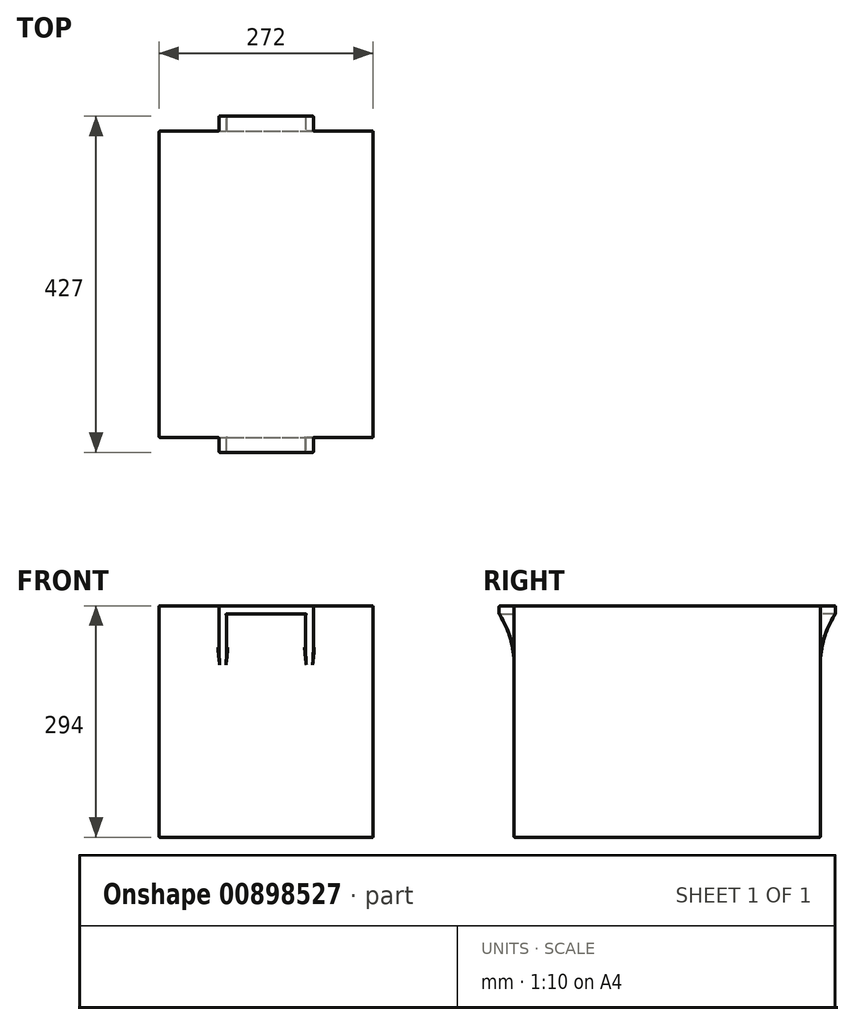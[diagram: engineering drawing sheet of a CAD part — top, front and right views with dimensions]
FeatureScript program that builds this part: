
annotation { "Feature Type Name" : "Feature", "Feature Type Description" : "" }
export const myFeature = defineFeature(function(context is Context, id is Id, definition is map)
    precondition{}
    {
        {
            var Q0;
            Q0=qCreatedBy(makeId("Top.planeOp"),FACE);
            var sketch = newSketch(context, id + "F0", { "sketchPlane" : qUnion([Q0])});
            skLineSegment(sketch, "E0.bottom", {"start": v(-136, 194.5) * mm, "end": v(0, 194.5) * mm});
            skLineSegment(sketch, "E0.left", {"start": v(-136, 194.5) * mm, "end": v(-136, 0) * mm});
            skLineSegment(sketch, "E1", {"start": v(0, 194.5) * mm, "end": v(0, 213.5) * mm});
            skLineSegment(sketch, "E2", {"start": v(0, 213.5) * mm, "end": v(0, 194.5) * mm});
            skLineSegment(sketch, "E3.right", {"start": v(-60, 213.5) * mm, "end": v(-60, 194.5) * mm});
            skPoint(sketch, "E3.middle", {"position": v(0, 194.5) * mm});
            skLineSegment(sketch, "E4", {"start": v(-136, 0) * mm, "end": v(0, 0) * mm});
            skLineSegment(sketch, "E5", {"start": v(0, 0) * mm, "end": v(0, 213.5) * mm});
            skLineSegment(sketch, "E6", {"start": v(-60, 213.5) * mm, "end": v(0, 213.5) * mm});
            skLineSegment(sketch, "E7", {"start": v(-60, 213.5) * mm, "end": v(-50, 213.5) * mm});
            skLineSegment(sketch, "E8", {"start": v(-50, 213.5) * mm, "end": v(-50, 194.5) * mm});
            skLineSegment(sketch, "E9", {"start": v(-50, 194.5) * mm, "end": v(-50, 213.5) * mm});
            skSolve(sketch);
        }
        {
            var Q0;
            {var subQ0=sQuery(id+"F0.wireOp",EDGE,"E0.left");Q0=makeQuery(id+"F0.imprint","IMPRINT",FACE,{"disambiguationData":[TD([[makeQuery(id+"F0.imprint","IMPRINT",EDGE,{"derivedFrom":subQ0}),1.0]])]});}
            extrude(context, id + "F1", {"entities" : qUnion([Q0]), "oppositeDirection" : true, "depth" : 294 * mm, "offsetDistance" : 25 * mm});
        }
        {
            var Q0;
            {var subQ4=sQuery(id+"F0.wireOp",EDGE,"E6");Q0=makeQuery(id+"F0.imprint","IMPRINT",FACE,{"disambiguationData":[TD([[makeQuery(id+"F0.imprint","IMPRINT",EDGE,{"derivedFrom":subQ4}),-1.0]])]});}
            extrude(context, id + "F2", {"entities" : qUnion([Q0]), "operationType" : NewBodyOperationType.ADD, "oppositeDirection" : true, "depth" : 10 * mm, "offsetDistance" : 25 * mm});
        }
        {
            var Q0;
            {var subQ0=sQuery(id+"F0.wireOp",EDGE,"E3.right");Q0=makeQuery(id+"F0.imprint","IMPRINT",FACE,{"disambiguationData":[TD([[makeQuery(id+"F0.imprint","IMPRINT",EDGE,{"derivedFrom":subQ0}),1.0]])]});}
            extrude(context, id + "F3", {"entities" : qUnion([Q0]), "operationType" : NewBodyOperationType.ADD, "oppositeDirection" : true, "depth" : 75 * mm, "offsetDistance" : 25 * mm});
        }
        {
            var Q0;
            Q0=makeQuery(id+"F3.opExtrude","SWEPT_FACE",FACE,{"disambiguationData":[OSD([sQuery(id+"F0.wireOp",EDGE,"E3.right")])]});
            var sketch = newSketch(context, id + "F4", { "sketchPlane" : qUnion([Q0])});
            skLineSegment(sketch, "E10.bottom", {"start": v(-213.5, 0) * mm, "end": v(-194.5, 0) * mm});
            skLineSegment(sketch, "E10.top", {"start": v(-213.5, -10) * mm, "end": v(-194.5, -10) * mm});
            skLineSegment(sketch, "E11.right", {"start": v(-194.5, -75) * mm, "end": v(-194.5, -10) * mm});
            skArc(sketch, "E12", {"start": v(-194.5, -75) * mm, "mid": v(-199.35, -41.14) * mm, "end": v(-213.5, -10) * mm});
            skSolve(sketch);
        }
        {
            var Q0;
            {var subQ0=sQuery(id+"F4.wireOp",EDGE,"E12");Q0=makeQuery(id+"F4.imprint","IMPRINT",FACE,{"disambiguationData":[TD([[makeQuery(id+"F4.imprint","IMPRINT",EDGE,{"derivedFrom":subQ0}),1.0]])]});}
            extrude(context, id + "F5", {"entities" : qUnion([Q0]), "operationType" : NewBodyOperationType.REMOVE, "oppositeDirection" : true, "depth" : 10 * mm, "offsetDistance" : 25 * mm});
        }
        {
            var Q0;
            Q0=makeQuery(id+"F1.opExtrude","SWEPT_BODY",BODY,{"disambiguationData":[OSD([sQuery(id+"F0.wireOp",EDGE,"E0.bottom"),sQuery(id+"F0.wireOp",EDGE,"E0.left"),sQuery(id+"F0.wireOp",EDGE,"E4"),sQuery(id+"F0.wireOp",EDGE,"E5")])]});
            var Q1;
            {var subQ0=sQuery(id+"F0.wireOp",EDGE,"E5");Q1=makeQuery(id+"F2.boolean.opBoolean","MERGE",FACE,{"derivedFrom":[makeQuery(id+"F1.opExtrude","SWEPT_FACE",FACE,{"disambiguationData":[OSD([subQ0])]}),makeQuery(id+"F2.opExtrude","SWEPT_FACE",FACE,{"disambiguationData":[OSD([subQ0])]})]});}
            mirror(context, id + "F6", {"operationType" : NewBodyOperationType.ADD, "entities" : qUnion([Q0]), "mirrorPlane" : qUnion([Q1])});
        }
        {
            var Q0;
            Q0=makeQuery(id+"F1.opExtrude","SWEPT_BODY",BODY,{"disambiguationData":[OSD([sQuery(id+"F0.wireOp",EDGE,"E0.bottom"),sQuery(id+"F0.wireOp",EDGE,"E0.left"),sQuery(id+"F0.wireOp",EDGE,"E4"),sQuery(id+"F0.wireOp",EDGE,"E5")])]});
            var Q1;
            {var subQ0=makeQuery(id+"F1.opExtrude","SWEPT_FACE",FACE,{"disambiguationData":[OSD([sQuery(id+"F0.wireOp",EDGE,"E4")])]});Q1=makeQuery(id+"F6.boolean.opBoolean","MERGE",FACE,{"derivedFrom":[subQ0,makeQuery(id+"F6.opPattern","COPY",FACE,{"derivedFrom":subQ0,"instanceName":"1"})]});}
            mirror(context, id + "F7", {"operationType" : NewBodyOperationType.ADD, "entities" : qUnion([Q0]), "mirrorPlane" : qUnion([Q1])});
        }
        {
            var Q0;
            {var subQ0=makeQuery(id+"F1.opExtrude","SWEPT_FACE",FACE,{"disambiguationData":[OSD([sQuery(id+"F0.wireOp",EDGE,"E0.bottom")])]});Q0=makeQuery(id+"F6.boolean.opBoolean","MERGE",FACE,{"derivedFrom":[subQ0,makeQuery(id+"F6.opPattern","COPY",FACE,{"derivedFrom":subQ0,"instanceName":"1"})]});}
            var Q1;
            Q1=makeQuery(id+"F6.opPattern","COPY",FACE,{"derivedFrom":makeQuery(id+"F5.boolean.opBoolean","COPY",FACE,{"derivedFrom":makeQuery(id+"F5.opExtrude","SWEPT_FACE",FACE,{"disambiguationData":[OSD([sQuery(id+"F4.wireOp",EDGE,"E12")])]})}),"instanceName":"1"});
            var Q2;
            Q2=makeQuery(id+"F6.opPattern","COPY",FACE,{"derivedFrom":makeQuery(id+"F3.opExtrude","SWEPT_FACE",FACE,{"disambiguationData":[OSD([sQuery(id+"F0.wireOp",EDGE,"E9")])]}),"instanceName":"1"});
            var Q3;
            {var subQ0=makeQuery(id+"F2.opExtrude","CAP_FACE",FACE,{"disambiguationData":[OSD([sQuery(id+"F0.wireOp",EDGE,"E0.bottom"),sQuery(id+"F0.wireOp",EDGE,"E5"),sQuery(id+"F0.wireOp",EDGE,"E6"),sQuery(id+"F0.wireOp",EDGE,"E9")])],"isStart":false});Q3=makeQuery(id+"F6.boolean.opBoolean","MERGE",FACE,{"derivedFrom":[subQ0,makeQuery(id+"F6.opPattern","COPY",FACE,{"derivedFrom":subQ0,"instanceName":"1"})]});}
            var Q4;
            {var subQ0=makeQuery(id+"F3.boolean.opBoolean","MERGE",FACE,{"derivedFrom":[makeQuery(id+"F2.opExtrude","SWEPT_FACE",FACE,{"disambiguationData":[OSD([sQuery(id+"F0.wireOp",EDGE,"E6")])]}),makeQuery(id+"F3.opExtrude","SWEPT_FACE",FACE,{"disambiguationData":[OSD([sQuery(id+"F0.wireOp",EDGE,"E7")])]})]});Q4=makeQuery(id+"F6.boolean.opBoolean","MERGE",FACE,{"derivedFrom":[subQ0,makeQuery(id+"F6.opPattern","COPY",FACE,{"derivedFrom":subQ0,"instanceName":"1"})]});}
            var Q5;
            Q5=makeQuery(id+"F5.boolean.opBoolean","COPY",FACE,{"derivedFrom":makeQuery(id+"F5.opExtrude","SWEPT_FACE",FACE,{"disambiguationData":[OSD([sQuery(id+"F4.wireOp",EDGE,"E12")])]})});
            var Q6;
            Q6=makeQuery(id+"F3.opExtrude","SWEPT_FACE",FACE,{"disambiguationData":[OSD([sQuery(id+"F0.wireOp",EDGE,"E9")])]});
            var Q7;
            Q7=makeQuery(id+"F6.opPattern","COPY",FACE,{"derivedFrom":makeQuery(id+"F3.opExtrude","SWEPT_FACE",FACE,{"disambiguationData":[OSD([sQuery(id+"F0.wireOp",EDGE,"E3.right")])]}),"instanceName":"1"});
            var Q8;
            Q8=makeQuery(id+"F3.opExtrude","SWEPT_FACE",FACE,{"disambiguationData":[OSD([sQuery(id+"F0.wireOp",EDGE,"E3.right")])]});
            var Q9;
            {var subQ0=sQuery(id+"F0.wireOp",EDGE,"E9");var subQ1=sQuery(id+"F0.wireOp",EDGE,"E0.bottom");var subQ2=sQuery(id+"F0.wireOp",EDGE,"E5");var subQ3=makeQuery(id+"F3.boolean.opBoolean","MERGE",FACE,{"derivedFrom":[makeQuery(id+"F2.boolean.opBoolean","MERGE",FACE,{"derivedFrom":[makeQuery(id+"F1.opExtrude","CAP_FACE",FACE,{"disambiguationData":[OSD([subQ1,sQuery(id+"F0.wireOp",EDGE,"E0.left"),sQuery(id+"F0.wireOp",EDGE,"E4"),subQ2])],"isStart":true}),makeQuery(id+"F2.opExtrude","CAP_FACE",FACE,{"disambiguationData":[OSD([subQ1,subQ2,sQuery(id+"F0.wireOp",EDGE,"E6"),subQ0])],"isStart":true})]}),makeQuery(id+"F3.opExtrude","CAP_FACE",FACE,{"disambiguationData":[OSD([subQ1,sQuery(id+"F0.wireOp",EDGE,"E3.right"),sQuery(id+"F0.wireOp",EDGE,"E7"),subQ0])],"isStart":true})]});var subQ4=makeQuery(id+"F6.boolean.opBoolean","MERGE",FACE,{"derivedFrom":[subQ3,makeQuery(id+"F6.opPattern","COPY",FACE,{"derivedFrom":subQ3,"instanceName":"1"})]});Q9=makeQuery(id+"F7.boolean.opBoolean","MERGE",FACE,{"derivedFrom":[subQ4,makeQuery(id+"F7.opPattern","COPY",FACE,{"derivedFrom":subQ4,"instanceName":"1"})]});}
            var Q10;
            {var subQ0=makeQuery(id+"F1.opExtrude","SWEPT_FACE",FACE,{"disambiguationData":[OSD([sQuery(id+"F0.wireOp",EDGE,"E0.left")])]});Q10=makeQuery(id+"F7.boolean.opBoolean","MERGE",FACE,{"derivedFrom":[subQ0,makeQuery(id+"F7.opPattern","COPY",FACE,{"derivedFrom":subQ0,"instanceName":"1"})]});}
            var Q11;
            {var subQ0=makeQuery(id+"F6.opPattern","COPY",FACE,{"derivedFrom":makeQuery(id+"F1.opExtrude","SWEPT_FACE",FACE,{"disambiguationData":[OSD([sQuery(id+"F0.wireOp",EDGE,"E0.left")])]}),"instanceName":"1"});Q11=makeQuery(id+"F7.boolean.opBoolean","MERGE",FACE,{"derivedFrom":[subQ0,makeQuery(id+"F7.opPattern","COPY",FACE,{"derivedFrom":subQ0,"instanceName":"1"})]});}
            var Q12;
            {var subQ0=makeQuery(id+"F1.opExtrude","SWEPT_FACE",FACE,{"disambiguationData":[OSD([sQuery(id+"F0.wireOp",EDGE,"E0.bottom")])]});Q12=makeQuery(id+"F7.opPattern","COPY",FACE,{"derivedFrom":makeQuery(id+"F6.boolean.opBoolean","MERGE",FACE,{"derivedFrom":[subQ0,makeQuery(id+"F6.opPattern","COPY",FACE,{"derivedFrom":subQ0,"instanceName":"1"})]}),"instanceName":"1"});}
            var Q13;
            Q13=makeQuery(id+"F7.opPattern","COPY",FACE,{"derivedFrom":makeQuery(id+"F6.opPattern","COPY",FACE,{"derivedFrom":makeQuery(id+"F3.opExtrude","SWEPT_FACE",FACE,{"disambiguationData":[OSD([sQuery(id+"F0.wireOp",EDGE,"E3.right")])]}),"instanceName":"1"}),"instanceName":"1"});
            var Q14;
            Q14=makeQuery(id+"F7.opPattern","COPY",FACE,{"derivedFrom":makeQuery(id+"F6.opPattern","COPY",FACE,{"derivedFrom":makeQuery(id+"F5.boolean.opBoolean","COPY",FACE,{"derivedFrom":makeQuery(id+"F5.opExtrude","SWEPT_FACE",FACE,{"disambiguationData":[OSD([sQuery(id+"F4.wireOp",EDGE,"E12")])]})}),"instanceName":"1"}),"instanceName":"1"});
            var Q15;
            {var subQ0=makeQuery(id+"F3.boolean.opBoolean","MERGE",FACE,{"derivedFrom":[makeQuery(id+"F2.opExtrude","SWEPT_FACE",FACE,{"disambiguationData":[OSD([sQuery(id+"F0.wireOp",EDGE,"E6")])]}),makeQuery(id+"F3.opExtrude","SWEPT_FACE",FACE,{"disambiguationData":[OSD([sQuery(id+"F0.wireOp",EDGE,"E7")])]})]});Q15=makeQuery(id+"F7.opPattern","COPY",FACE,{"derivedFrom":makeQuery(id+"F6.boolean.opBoolean","MERGE",FACE,{"derivedFrom":[subQ0,makeQuery(id+"F6.opPattern","COPY",FACE,{"derivedFrom":subQ0,"instanceName":"1"})]}),"instanceName":"1"});}
            var Q16;
            Q16=makeQuery(id+"F7.opPattern","COPY",FACE,{"derivedFrom":makeQuery(id+"F6.opPattern","COPY",FACE,{"derivedFrom":makeQuery(id+"F3.opExtrude","SWEPT_FACE",FACE,{"disambiguationData":[OSD([sQuery(id+"F0.wireOp",EDGE,"E9")])]}),"instanceName":"1"}),"instanceName":"1"});
            var Q17;
            {var subQ0=makeQuery(id+"F2.opExtrude","CAP_FACE",FACE,{"disambiguationData":[OSD([sQuery(id+"F0.wireOp",EDGE,"E0.bottom"),sQuery(id+"F0.wireOp",EDGE,"E5"),sQuery(id+"F0.wireOp",EDGE,"E6"),sQuery(id+"F0.wireOp",EDGE,"E9")])],"isStart":false});Q17=makeQuery(id+"F7.opPattern","COPY",FACE,{"derivedFrom":makeQuery(id+"F6.boolean.opBoolean","MERGE",FACE,{"derivedFrom":[subQ0,makeQuery(id+"F6.opPattern","COPY",FACE,{"derivedFrom":subQ0,"instanceName":"1"})]}),"instanceName":"1"});}
            var Q18;
            Q18=makeQuery(id+"F7.opPattern","COPY",FACE,{"derivedFrom":makeQuery(id+"F3.opExtrude","SWEPT_FACE",FACE,{"disambiguationData":[OSD([sQuery(id+"F0.wireOp",EDGE,"E9")])]}),"instanceName":"1"});
            var Q19;
            Q19=makeQuery(id+"F7.opPattern","COPY",FACE,{"derivedFrom":makeQuery(id+"F5.boolean.opBoolean","COPY",FACE,{"derivedFrom":makeQuery(id+"F5.opExtrude","SWEPT_FACE",FACE,{"disambiguationData":[OSD([sQuery(id+"F4.wireOp",EDGE,"E12")])]})}),"instanceName":"1"});
            var Q20;
            Q20=makeQuery(id+"F7.opPattern","COPY",FACE,{"derivedFrom":makeQuery(id+"F3.opExtrude","SWEPT_FACE",FACE,{"disambiguationData":[OSD([sQuery(id+"F0.wireOp",EDGE,"E3.right")])]}),"instanceName":"1"});
            var Q21;
            {var subQ0=makeQuery(id+"F1.opExtrude","CAP_FACE",FACE,{"disambiguationData":[OSD([sQuery(id+"F0.wireOp",EDGE,"E0.bottom"),sQuery(id+"F0.wireOp",EDGE,"E0.left"),sQuery(id+"F0.wireOp",EDGE,"E4"),sQuery(id+"F0.wireOp",EDGE,"E5")])],"isStart":false});var subQ1=makeQuery(id+"F6.boolean.opBoolean","MERGE",FACE,{"derivedFrom":[subQ0,makeQuery(id+"F6.opPattern","COPY",FACE,{"derivedFrom":subQ0,"instanceName":"1"})]});Q21=makeQuery(id+"F7.boolean.opBoolean","MERGE",FACE,{"derivedFrom":[subQ1,makeQuery(id+"F7.opPattern","COPY",FACE,{"derivedFrom":subQ1,"instanceName":"1"})]});}
            fillet(context, id + "F8", {"entities" : qUnion([Q0, Q1, Q2, Q3, Q4, Q5, Q6, Q7, Q8, Q9, Q10, Q11, Q12, Q13, Q14, Q15, Q16, Q17, Q18, Q19, Q20, Q21]), "radius" : 1 * mm, "tangentPropagation" : true, "allowEdgeOverflow" : false});
        }
    });
